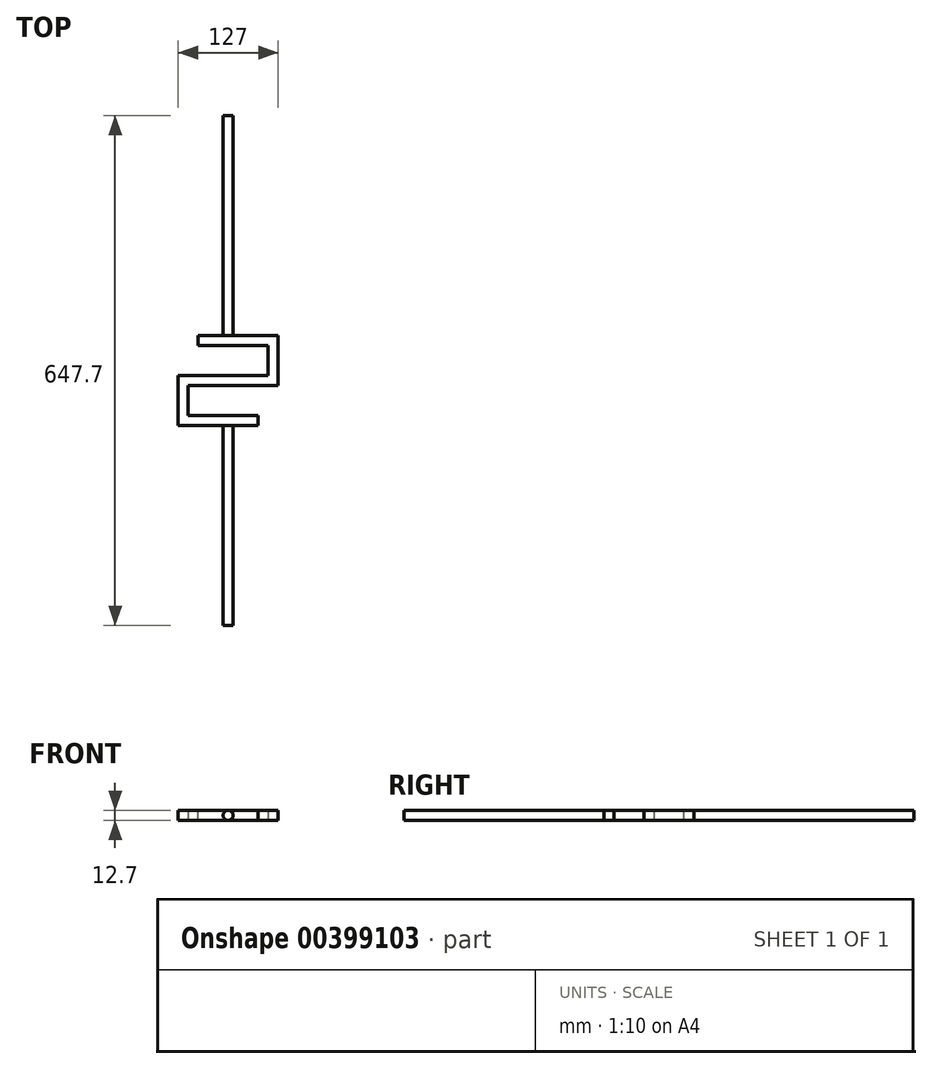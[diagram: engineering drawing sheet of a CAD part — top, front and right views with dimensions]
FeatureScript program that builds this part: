
annotation { "Feature Type Name" : "Feature", "Feature Type Description" : "" }
export const myFeature = defineFeature(function(context is Context, id is Id, definition is map)
    precondition{}
    {
        {
            var Q0;
            Q0=qCreatedBy(makeId("Right.planeOp"),FACE);
            var sketch = newSketch(context, id + "F0", { "sketchPlane" : qUnion([Q0])});
            skLineSegment(sketch, "E0.bottom", {"start": v(0, 0) * mm, "end": v(-12.7, 0) * mm});
            skLineSegment(sketch, "E0.top", {"start": v(0, -12.7) * mm, "end": v(-12.7, -12.7) * mm});
            skLineSegment(sketch, "E0.left", {"start": v(0, 0) * mm, "end": v(0, -12.7) * mm});
            skLineSegment(sketch, "E0.right", {"start": v(-12.7, 0) * mm, "end": v(-12.7, -12.7) * mm});
            skSolve(sketch);
        }
        {
            var Q0;
            Q0=makeQuery(id+"F0.imprint","IMPRINT",FACE,{"disambiguationData":[TD([[makeQuery(id+"F0.imprint","IMPRINT",EDGE,{"derivedFrom":sQuery(id+"F0.wireOp",EDGE,"E0.bottom")}),1.0]])]});
            extrude(context, id + "F1", {"entities" : qUnion([Q0]), "depth" : 101.6 * mm});
        }
        {
            var Q0;
            Q0=makeQuery(id+"F1.opExtrude","CAP_FACE",FACE,{"disambiguationData":[OSD([sQuery(id+"F0.wireOp",EDGE,"E0.bottom"),sQuery(id+"F0.wireOp",EDGE,"E0.top"),sQuery(id+"F0.wireOp",EDGE,"E0.left"),sQuery(id+"F0.wireOp",EDGE,"E0.right")])],"isStart":false});
            var sketch = newSketch(context, id + "F2", { "sketchPlane" : qUnion([Q0])});
            skLineSegment(sketch, "E1.bottom", {"start": v(-12.7, -12.7) * mm, "end": v(38.1, -12.7) * mm});
            skLineSegment(sketch, "E1.top", {"start": v(-12.7, 0) * mm, "end": v(38.1, 0) * mm});
            skLineSegment(sketch, "E1.left", {"start": v(-12.7, -12.7) * mm, "end": v(-12.7, 0) * mm});
            skLineSegment(sketch, "E1.right", {"start": v(38.1, -12.7) * mm, "end": v(38.1, 0) * mm});
            skSolve(sketch);
        }
        {
            var Q0;
            {var subQ2=sQuery(id+"F2.wireOp",EDGE,"E1.right");Q0=makeQuery(id+"F2.imprint","IMPRINT",FACE,{"disambiguationData":[TD([[makeQuery(id+"F2.imprint","IMPRINT",EDGE,{"derivedFrom":subQ2}),1.0]])]});}
            var Q1;
            {var subQ2=sQuery(id+"F2.wireOp",EDGE,"E1.left");Q1=makeQuery(id+"F2.imprint","IMPRINT",FACE,{"disambiguationData":[TD([[makeQuery(id+"F2.imprint","IMPRINT",EDGE,{"derivedFrom":subQ2}),1.0]])]});}
            extrude(context, id + "F3", {"entities" : qUnion([Q0, Q1]), "operationType" : NewBodyOperationType.ADD, "depth" : 12.7 * mm});
        }
        {
            var Q0;
            Q0=makeQuery(id+"F1.opExtrude","CAP_FACE",FACE,{"disambiguationData":[OSD([sQuery(id+"F0.wireOp",EDGE,"E0.bottom"),sQuery(id+"F0.wireOp",EDGE,"E0.top"),sQuery(id+"F0.wireOp",EDGE,"E0.left"),sQuery(id+"F0.wireOp",EDGE,"E0.right")])],"isStart":true});
            var sketch = newSketch(context, id + "F4", { "sketchPlane" : qUnion([Q0])});
            skLineSegment(sketch, "E2.bottom", {"start": v(0, 0) * mm, "end": v(50.8, 0) * mm});
            skLineSegment(sketch, "E2.top", {"start": v(0, -12.7) * mm, "end": v(50.8, -12.7) * mm});
            skLineSegment(sketch, "E2.left", {"start": v(0, 0) * mm, "end": v(0, -12.7) * mm});
            skLineSegment(sketch, "E2.right", {"start": v(50.8, 0) * mm, "end": v(50.8, -12.7) * mm});
            skSolve(sketch);
        }
        {
            var Q0;
            {var subQ2=sQuery(id+"F4.wireOp",EDGE,"E2.right");Q0=makeQuery(id+"F4.imprint","IMPRINT",FACE,{"disambiguationData":[TD([[makeQuery(id+"F4.imprint","IMPRINT",EDGE,{"derivedFrom":subQ2}),-1.0]])]});}
            var Q1;
            {var subQ0=sQuery(id+"F4.wireOp",EDGE,"E2.left");Q1=makeQuery(id+"F4.imprint","IMPRINT",FACE,{"disambiguationData":[TD([[makeQuery(id+"F4.imprint","IMPRINT",EDGE,{"derivedFrom":subQ0}),1.0]])]});}
            extrude(context, id + "F5", {"entities" : qUnion([Q0, Q1]), "operationType" : NewBodyOperationType.ADD, "depth" : 12.7 * mm});
        }
        {
            var Q0;
            Q0=makeQuery(id+"F5.opExtrude","SWEPT_FACE",FACE,{"disambiguationData":[OSD([sQuery(id+"F4.wireOp",EDGE,"E2.right")])]});
            var sketch = newSketch(context, id + "F6", { "sketchPlane" : qUnion([Q0])});
            skLineSegment(sketch, "E3.bottom", {"start": v(-12.7, 0) * mm, "end": v(88.9, 0) * mm});
            skLineSegment(sketch, "E3.top", {"start": v(-12.7, -12.7) * mm, "end": v(88.9, -12.7) * mm});
            skLineSegment(sketch, "E3.left", {"start": v(-12.7, 0) * mm, "end": v(-12.7, -12.7) * mm});
            skLineSegment(sketch, "E3.right", {"start": v(88.9, 0) * mm, "end": v(88.9, -12.7) * mm});
            skSolve(sketch);
        }
        {
            var Q0;
            {var subQ2=sQuery(id+"F6.wireOp",EDGE,"E3.right");Q0=makeQuery(id+"F6.imprint","IMPRINT",FACE,{"disambiguationData":[TD([[makeQuery(id+"F6.imprint","IMPRINT",EDGE,{"derivedFrom":subQ2}),-1.0]])]});}
            var Q1;
            {var subQ2=sQuery(id+"F6.wireOp",EDGE,"E3.left");Q1=makeQuery(id+"F6.imprint","IMPRINT",FACE,{"disambiguationData":[TD([[makeQuery(id+"F6.imprint","IMPRINT",EDGE,{"derivedFrom":subQ2}),1.0]])]});}
            extrude(context, id + "F7", {"entities" : qUnion([Q0, Q1]), "operationType" : NewBodyOperationType.ADD, "depth" : 12.7 * mm});
        }
        {
            var Q0;
            Q0=makeQuery(id+"F3.opExtrude","SWEPT_FACE",FACE,{"disambiguationData":[OSD([sQuery(id+"F2.wireOp",EDGE,"E1.right")])]});
            var sketch = newSketch(context, id + "F8", { "sketchPlane" : qUnion([Q0])});
            skLineSegment(sketch, "E4.bottom", {"start": v(-114.3, -12.7) * mm, "end": v(-12.7, -12.7) * mm});
            skLineSegment(sketch, "E4.top", {"start": v(-114.3, 0) * mm, "end": v(-12.7, 0) * mm});
            skLineSegment(sketch, "E4.left", {"start": v(-114.3, -12.7) * mm, "end": v(-114.3, 0) * mm});
            skLineSegment(sketch, "E4.right", {"start": v(-12.7, -12.7) * mm, "end": v(-12.7, 0) * mm});
            skSolve(sketch);
        }
        {
            var Q0;
            {var subQ2=sQuery(id+"F8.wireOp",EDGE,"E4.right");Q0=makeQuery(id+"F8.imprint","IMPRINT",FACE,{"disambiguationData":[TD([[makeQuery(id+"F8.imprint","IMPRINT",EDGE,{"derivedFrom":subQ2}),1.0]])]});}
            var Q1;
            {var subQ2=sQuery(id+"F8.wireOp",EDGE,"E4.left");Q1=makeQuery(id+"F8.imprint","IMPRINT",FACE,{"disambiguationData":[TD([[makeQuery(id+"F8.imprint","IMPRINT",EDGE,{"derivedFrom":subQ2}),-1.0]])]});}
            extrude(context, id + "F9", {"entities" : qUnion([Q0, Q1]), "operationType" : NewBodyOperationType.ADD, "depth" : 12.7 * mm});
        }
        {
            var Q0;
            Q0=makeQuery(id+"F7.opExtrude","CAP_FACE",FACE,{"disambiguationData":[OSD([sQuery(id+"F6.wireOp",EDGE,"E3.bottom"),sQuery(id+"F6.wireOp",EDGE,"E3.top"),sQuery(id+"F6.wireOp",EDGE,"E3.left"),sQuery(id+"F6.wireOp",EDGE,"E3.right")])],"isStart":false});
            var sketch = newSketch(context, id + "F10", { "sketchPlane" : qUnion([Q0])});
            skCircle(sketch, "E5", {"center": v(50.8, -6.35) * mm, "radius": 6.35 * mm});
            skPoint(sketch, "E5.centerSnap0", {"position": v(88.9, -6.35) * mm});
            skSolve(sketch);
        }
        {
            var Q0;
            {var subQ0=sQuery(id+"F10.wireOp",EDGE,"E5");var subQ1=makeQuery(id+"F10.imprint","INTERSECT",VERTEX,{"derivedFrom":[makeQuery(id+"F7.opExtrude","CAP_EDGE",EDGE,{"disambiguationData":[OSD([sQuery(id+"F6.wireOp",EDGE,"E3.bottom")])],"isStart":false}),subQ0]});Q0=makeQuery(id+"F10.imprint","IMPRINT",FACE,{"disambiguationData":[TD([[makeQuery(id+"F10.imprint","IMPRINT",EDGE,{"disambiguationData":[TD([[subQ1,-1.0]])],"derivedFrom":subQ0}),1.0]])]});}
            extrude(context, id + "F11", {"entities" : qUnion([Q0]), "operationType" : NewBodyOperationType.ADD, "depth" : 254 * mm});
        }
        {
            var Q0;
            Q0=makeQuery(id+"F9.opExtrude","CAP_FACE",FACE,{"disambiguationData":[OSD([sQuery(id+"F8.wireOp",EDGE,"E4.bottom"),sQuery(id+"F8.wireOp",EDGE,"E4.top"),sQuery(id+"F8.wireOp",EDGE,"E4.left"),sQuery(id+"F8.wireOp",EDGE,"E4.right")])],"isStart":false});
            var sketch = newSketch(context, id + "F12", { "sketchPlane" : qUnion([Q0])});
            skCircle(sketch, "E6", {"center": v(-50.8, -6.35) * mm, "radius": 6.35 * mm});
            skPoint(sketch, "E6.centerSnap0", {"position": v(-12.7, -6.35) * mm});
            skSolve(sketch);
        }
        {
            var Q0;
            {var subQ0=sQuery(id+"F12.wireOp",EDGE,"E6");var subQ1=makeQuery(id+"F12.imprint","INTERSECT",VERTEX,{"derivedFrom":[makeQuery(id+"F9.opExtrude","CAP_EDGE",EDGE,{"disambiguationData":[OSD([sQuery(id+"F8.wireOp",EDGE,"E4.bottom")])],"isStart":false}),subQ0]});Q0=makeQuery(id+"F12.imprint","IMPRINT",FACE,{"disambiguationData":[TD([[makeQuery(id+"F12.imprint","IMPRINT",EDGE,{"disambiguationData":[TD([[subQ1,1.0]])],"derivedFrom":subQ0}),1.0]])]});}
            extrude(context, id + "F13", {"entities" : qUnion([Q0]), "operationType" : NewBodyOperationType.ADD, "depth" : 279.4 * mm});
        }
    });
